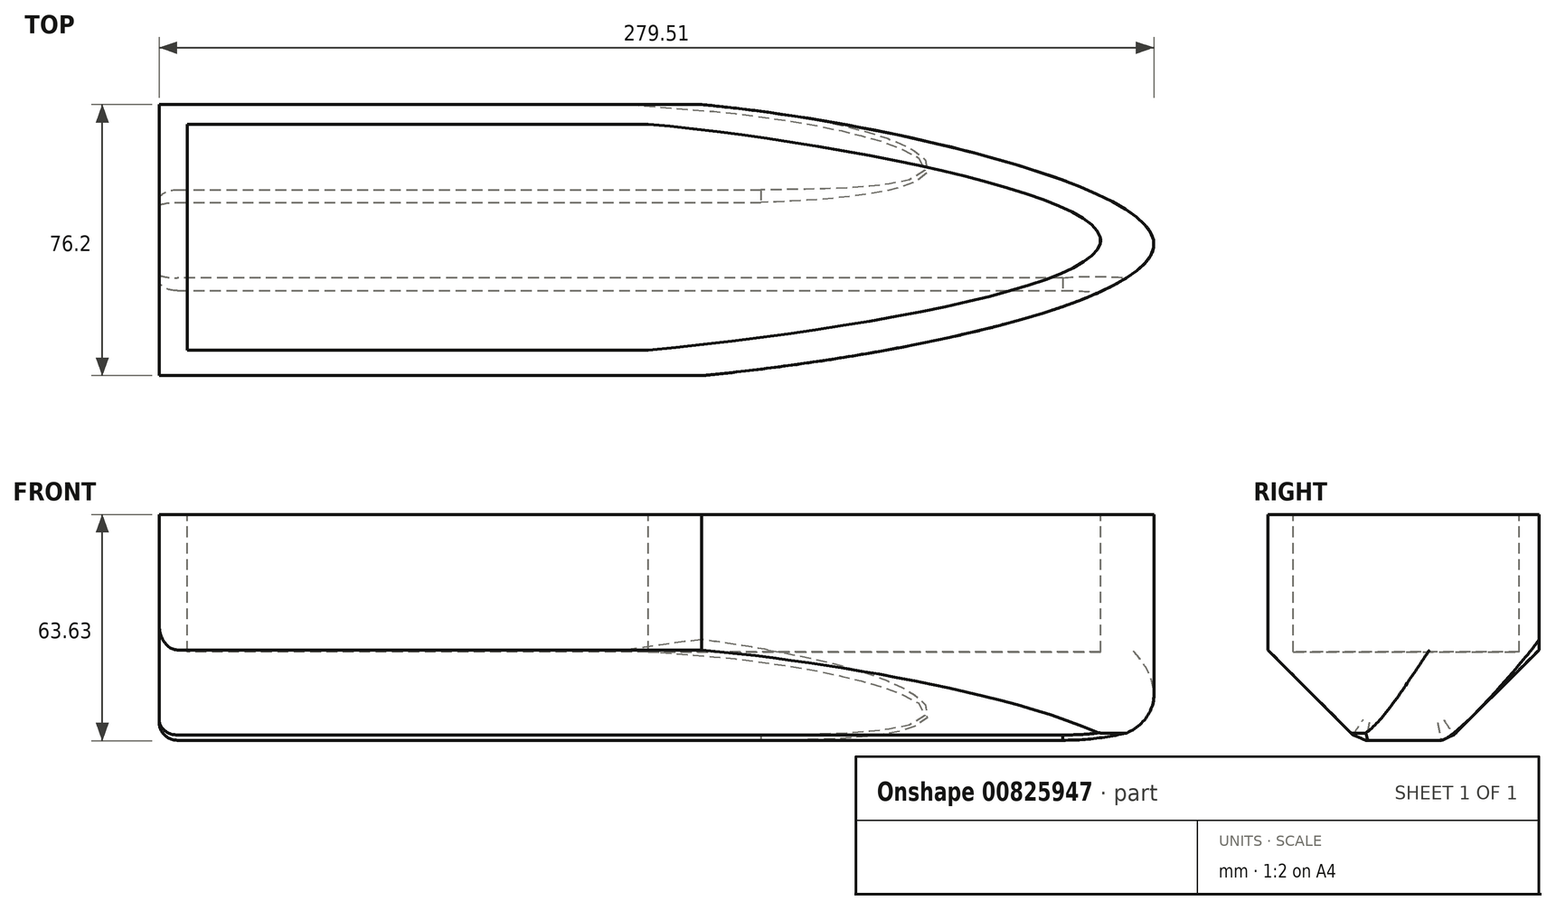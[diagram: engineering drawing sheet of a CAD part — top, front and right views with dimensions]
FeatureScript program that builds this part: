
annotation { "Feature Type Name" : "Feature", "Feature Type Description" : "" }
export const myFeature = defineFeature(function(context is Context, id is Id, definition is map)
    precondition{}
    {
        {
            var Q0;
            Q0=qCreatedBy(makeId("Top.planeOp"),FACE);
            var sketch = newSketch(context, id + "F0", { "sketchPlane" : qUnion([Q0])});
            skLineSegment(sketch, "E0.bottom", {"start": v(61.78, 12.87) * mm, "end": v(-90.62, 12.87) * mm});
            skLineSegment(sketch, "E0.top", {"start": v(61.78, -63.33) * mm, "end": v(-90.62, -63.33) * mm});
            skLineSegment(sketch, "E0.left", {"start": v(61.78, 12.87) * mm, "end": v(61.78, -63.33) * mm});
            skLineSegment(sketch, "E0.right", {"start": v(-90.62, 12.87) * mm, "end": v(-90.62, -63.33) * mm});
            skFitSpline(sketch, "E1", {"points": [v(61.78, -63.33) * mm, v(188.78, -25.23) * mm, v(61.78, 12.87) * mm], "startDerivative": vector(352.28, 33.67) * mm, "endDerivative": vector(-275.15, 24.34) * mm});
            skLineSegment(sketch, "E2", {"start": v(61.78, -25.23) * mm, "end": v(188.78, -25.23) * mm});
            skSolve(sketch);
        }
        {
            var Q0;
            Q0 = qSketchRegion(id + "F0", true);
            extrude(context, id + "F1", {"entities" : qUnion([Q0]), "depth" : 63.5 * mm, "offsetDistance" : 25.4 * mm});
        }
        {
            var Q0;
            Q0=makeQuery(id+"F1.opExtrude","CAP_EDGE",EDGE,{"disambiguationData":[OSD([sQuery(id+"F0.wireOp",EDGE,"E0.bottom")])],"isStart":true});
            var Q1;
            Q1=makeQuery(id+"F1.opExtrude","CAP_EDGE",EDGE,{"disambiguationData":[OSD([sQuery(id+"F0.wireOp",EDGE,"E0.top")])],"isStart":true});
            chamfer(context, id + "F2", {"entities" : qUnion([Q0, Q1]), "width" : 25.4 * mm, "tangentPropagation" : true});
        }
        {
            var Q0;
            Q0=makeQuery(id+"F1.opExtrude","CAP_EDGE",EDGE,{"disambiguationData":[OSD([sQuery(id+"F0.wireOp",EDGE,"E1")])],"isStart":true});
            fillet(context, id + "F3", {"entities" : qUnion([Q0]), "radius" : 25.4 * mm, "tangentPropagation" : true, "allowEdgeOverflow" : false});
        }
        {
            var Q0;
            {var subQ0=sQuery(id+"F0.wireOp",EDGE,"E0.bottom");Q0=makeQuery(id+"F2.opChamfer","BLEND_EDGE",EDGE,{"blendedFrom":[makeQuery(id+"F1.opExtrude","CAP_EDGE",EDGE,{"disambiguationData":[OSD([subQ0])],"isStart":true}),makeQuery(id+"F1.opExtrude","CAP_FACE",FACE,{"disambiguationData":[OSD([subQ0,sQuery(id+"F0.wireOp",EDGE,"E0.top"),sQuery(id+"F0.wireOp",EDGE,"E0.right"),sQuery(id+"F0.wireOp",EDGE,"E1")])],"isStart":true})],"blendedInto":[makeQuery(id+"F1.opExtrude","CAP_FACE",FACE,{"disambiguationData":[OSD([subQ0,sQuery(id+"F0.wireOp",EDGE,"E0.top"),sQuery(id+"F0.wireOp",EDGE,"E0.right"),sQuery(id+"F0.wireOp",EDGE,"E1")])],"isStart":true})]});}
            var Q1;
            {var subQ0=sQuery(id+"F0.wireOp",EDGE,"E0.top");Q1=makeQuery(id+"F2.opChamfer","BLEND_EDGE",EDGE,{"blendedFrom":[makeQuery(id+"F1.opExtrude","CAP_EDGE",EDGE,{"disambiguationData":[OSD([subQ0])],"isStart":true}),makeQuery(id+"F1.opExtrude","CAP_FACE",FACE,{"disambiguationData":[OSD([sQuery(id+"F0.wireOp",EDGE,"E0.bottom"),subQ0,sQuery(id+"F0.wireOp",EDGE,"E0.right"),sQuery(id+"F0.wireOp",EDGE,"E1")])],"isStart":true})],"blendedInto":[makeQuery(id+"F1.opExtrude","CAP_FACE",FACE,{"disambiguationData":[OSD([sQuery(id+"F0.wireOp",EDGE,"E0.bottom"),subQ0,sQuery(id+"F0.wireOp",EDGE,"E0.right"),sQuery(id+"F0.wireOp",EDGE,"E1")])],"isStart":true})]});}
            chamfer(context, id + "F4", {"entities" : qUnion([Q0, Q1]), "width" : 5.08 * mm, "tangentPropagation" : true});
        }
        {
            var Q0;
            Q0=makeQuery(id+"F2.opChamfer","BLEND_EDGE",EDGE,{"blendedFrom":[makeQuery(id+"F1.opExtrude","CAP_EDGE",EDGE,{"disambiguationData":[OSD([sQuery(id+"F0.wireOp",EDGE,"E0.bottom")])],"isStart":true}),makeQuery(id+"F1.opExtrude","SWEPT_FACE",FACE,{"disambiguationData":[OSD([sQuery(id+"F0.wireOp",EDGE,"E0.right")])]})],"blendedInto":[makeQuery(id+"F1.opExtrude","SWEPT_FACE",FACE,{"disambiguationData":[OSD([sQuery(id+"F0.wireOp",EDGE,"E0.right")])]})]});
            var Q1;
            {var subQ0=sQuery(id+"F0.wireOp",EDGE,"E0.right");var subQ1=sQuery(id+"F0.wireOp",EDGE,"E0.bottom");Q1=makeQuery(id+"F4.opChamfer","BLEND_EDGE",EDGE,{"blendedFrom":[makeQuery(id+"F2.opChamfer","BLEND_EDGE",EDGE,{"blendedFrom":[makeQuery(id+"F1.opExtrude","CAP_EDGE",EDGE,{"disambiguationData":[OSD([subQ1])],"isStart":true}),makeQuery(id+"F1.opExtrude","CAP_FACE",FACE,{"disambiguationData":[OSD([subQ1,sQuery(id+"F0.wireOp",EDGE,"E0.top"),subQ0,sQuery(id+"F0.wireOp",EDGE,"E1")])],"isStart":true})],"blendedInto":[makeQuery(id+"F1.opExtrude","CAP_FACE",FACE,{"disambiguationData":[OSD([subQ1,sQuery(id+"F0.wireOp",EDGE,"E0.top"),subQ0,sQuery(id+"F0.wireOp",EDGE,"E1")])],"isStart":true})]}),makeQuery(id+"F1.opExtrude","SWEPT_FACE",FACE,{"disambiguationData":[OSD([subQ0])]})],"blendedInto":[makeQuery(id+"F1.opExtrude","SWEPT_FACE",FACE,{"disambiguationData":[OSD([subQ0])]})]});}
            var Q2;
            Q2=makeQuery(id+"F1.opExtrude","CAP_EDGE",EDGE,{"disambiguationData":[OSD([sQuery(id+"F0.wireOp",EDGE,"E0.right")])],"isStart":true});
            var Q3;
            {var subQ0=sQuery(id+"F0.wireOp",EDGE,"E0.right");var subQ1=sQuery(id+"F0.wireOp",EDGE,"E0.top");Q3=makeQuery(id+"F4.opChamfer","BLEND_EDGE",EDGE,{"blendedFrom":[makeQuery(id+"F2.opChamfer","BLEND_EDGE",EDGE,{"blendedFrom":[makeQuery(id+"F1.opExtrude","CAP_EDGE",EDGE,{"disambiguationData":[OSD([subQ1])],"isStart":true}),makeQuery(id+"F1.opExtrude","CAP_FACE",FACE,{"disambiguationData":[OSD([sQuery(id+"F0.wireOp",EDGE,"E0.bottom"),subQ1,subQ0,sQuery(id+"F0.wireOp",EDGE,"E1")])],"isStart":true})],"blendedInto":[makeQuery(id+"F1.opExtrude","CAP_FACE",FACE,{"disambiguationData":[OSD([sQuery(id+"F0.wireOp",EDGE,"E0.bottom"),subQ1,subQ0,sQuery(id+"F0.wireOp",EDGE,"E1")])],"isStart":true})]}),makeQuery(id+"F1.opExtrude","SWEPT_FACE",FACE,{"disambiguationData":[OSD([subQ0])]})],"blendedInto":[makeQuery(id+"F1.opExtrude","SWEPT_FACE",FACE,{"disambiguationData":[OSD([subQ0])]})]});}
            var Q4;
            Q4=makeQuery(id+"F2.opChamfer","BLEND_EDGE",EDGE,{"blendedFrom":[makeQuery(id+"F1.opExtrude","CAP_EDGE",EDGE,{"disambiguationData":[OSD([sQuery(id+"F0.wireOp",EDGE,"E0.top")])],"isStart":true}),makeQuery(id+"F1.opExtrude","SWEPT_FACE",FACE,{"disambiguationData":[OSD([sQuery(id+"F0.wireOp",EDGE,"E0.right")])]})],"blendedInto":[makeQuery(id+"F1.opExtrude","SWEPT_FACE",FACE,{"disambiguationData":[OSD([sQuery(id+"F0.wireOp",EDGE,"E0.right")])]})]});
            fillet(context, id + "F5", {"entities" : qUnion([Q0, Q1, Q2, Q3, Q4]), "radius" : 5.08 * mm, "tangentPropagation" : true, "allowEdgeOverflow" : false});
        }
        {
            var Q0;
            Q0=makeQuery(id+"F1.opExtrude","CAP_FACE",FACE,{"disambiguationData":[OSD([sQuery(id+"F0.wireOp",EDGE,"E0.bottom"),sQuery(id+"F0.wireOp",EDGE,"E0.top"),sQuery(id+"F0.wireOp",EDGE,"E0.right"),sQuery(id+"F0.wireOp",EDGE,"E1")])],"isStart":false});
            var sketch = newSketch(context, id + "F6", { "sketchPlane" : qUnion([Q0])});
            skLineSegment(sketch, "E3.bottom", {"start": v(46.81, 7.36) * mm, "end": v(-82.73, 7.36) * mm});
            skLineSegment(sketch, "E3.top", {"start": v(46.81, -56.14) * mm, "end": v(-82.73, -56.14) * mm});
            skLineSegment(sketch, "E3.left", {"start": v(46.81, 7.36) * mm, "end": v(46.81, -56.14) * mm});
            skLineSegment(sketch, "E3.right", {"start": v(-82.73, 7.36) * mm, "end": v(-82.73, -56.14) * mm});
            skFitSpline(sketch, "E4", {"points": [v(46.81, -56.14) * mm, v(173.81, -24.4) * mm, v(46.81, 7.36) * mm], "startDerivative": vector(352.28, 33.67) * mm, "endDerivative": vector(-275.15, 24.34) * mm});
            skLineSegment(sketch, "E5", {"start": v(46.81, -24.4) * mm, "end": v(173.81, -24.4) * mm});
            skSolve(sketch);
        }
        {
            var Q0;
            Q0 = qSketchRegion(id + "F6", true);
            extrude(context, id + "F7", {"entities" : qUnion([Q0]), "operationType" : NewBodyOperationType.REMOVE, "oppositeDirection" : true, "depth" : 38.6 * mm, "offsetDistance" : 25.4 * mm});
        }
    });
